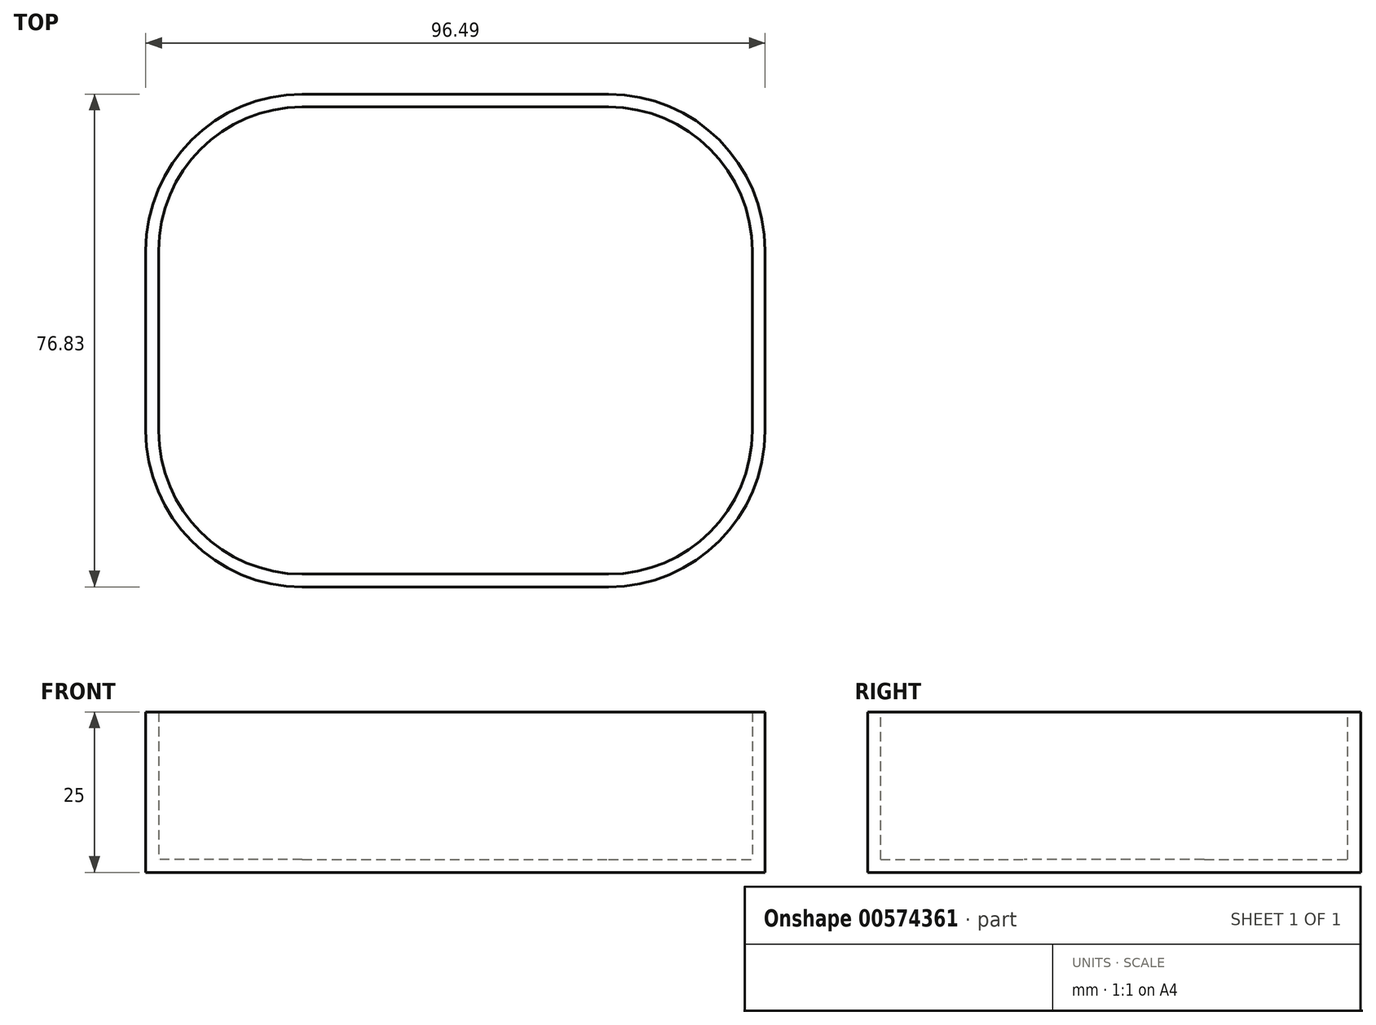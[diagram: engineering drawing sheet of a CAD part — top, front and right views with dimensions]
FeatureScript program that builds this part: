
annotation { "Feature Type Name" : "Feature", "Feature Type Description" : "" }
export const myFeature = defineFeature(function(context is Context, id is Id, definition is map)
    precondition{}
    {
        {
            var Q0;
            Q0=qCreatedBy(makeId("Top.planeOp"),FACE);
            var sketch = newSketch(context, id + "F0", { "sketchPlane" : qUnion([Q0])});
            skLineSegment(sketch, "E0.bottom", {"start": v(-49.71, 35.14) * mm, "end": v(46.78, 35.14) * mm});
            skLineSegment(sketch, "E0.top", {"start": v(-49.71, -41.7) * mm, "end": v(46.78, -41.7) * mm});
            skLineSegment(sketch, "E0.left", {"start": v(-49.71, 35.14) * mm, "end": v(-49.71, -41.7) * mm});
            skLineSegment(sketch, "E0.right", {"start": v(46.78, 35.14) * mm, "end": v(46.78, -41.7) * mm});
            skSolve(sketch);
        }
        {
            var Q0;
            Q0 = qSketchRegion(id + "F0", true);
            extrude(context, id + "F1", {"entities" : qUnion([Q0]), "depth" : 25 * mm, "offsetDistance" : 25 * mm});
        }
        {
            var Q0;
            Q0=makeQuery(id+"F1.opExtrude","SWEPT_EDGE",EDGE,{"disambiguationData":[OSD([sQuery(id+"F0.wireOp",EDGE,"E0.top"),sQuery(id+"F0.wireOp",EDGE,"E0.right")])]});
            var Q1;
            Q1=makeQuery(id+"F1.opExtrude","SWEPT_EDGE",EDGE,{"disambiguationData":[OSD([sQuery(id+"F0.wireOp",EDGE,"E0.bottom"),sQuery(id+"F0.wireOp",EDGE,"E0.right")])]});
            var Q2;
            Q2=makeQuery(id+"F1.opExtrude","SWEPT_EDGE",EDGE,{"disambiguationData":[OSD([sQuery(id+"F0.wireOp",EDGE,"E0.bottom"),sQuery(id+"F0.wireOp",EDGE,"E0.left")])]});
            var Q3;
            Q3=makeQuery(id+"F1.opExtrude","SWEPT_EDGE",EDGE,{"disambiguationData":[OSD([sQuery(id+"F0.wireOp",EDGE,"E0.top"),sQuery(id+"F0.wireOp",EDGE,"E0.left")])]});
            fillet(context, id + "F2", {"entities" : qUnion([Q0, Q1, Q2, Q3]), "radius" : 24.38 * mm, "tangentPropagation" : true, "allowEdgeOverflow" : false});
        }
        {
            var Q0;
            Q0=makeQuery(id+"F1.opExtrude","CAP_FACE",FACE,{"disambiguationData":[OSD([sQuery(id+"F0.wireOp",EDGE,"E0.bottom"),sQuery(id+"F0.wireOp",EDGE,"E0.top"),sQuery(id+"F0.wireOp",EDGE,"E0.left"),sQuery(id+"F0.wireOp",EDGE,"E0.right")])],"isStart":false});
            shell(context, id + "F3", {"entities" : qUnion([Q0]), "thickness" : 2 * mm});
        }
    });
